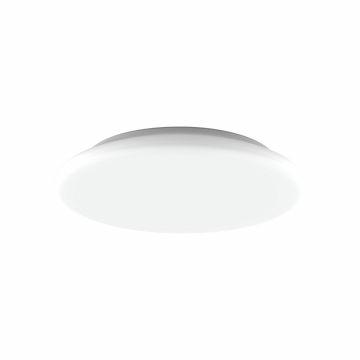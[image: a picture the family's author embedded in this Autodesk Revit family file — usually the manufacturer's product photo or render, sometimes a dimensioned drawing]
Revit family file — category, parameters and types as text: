
# Revit family: Lighting-CommercialSector-GEWISS-ELIA-CL-LED_CEILING_D250
name_source: partatom
category: Apparecchi per illuminazione
units: mm (PartAtom-declared; Revit-internal decimal feet)

## family parameters
Condiviso = No
Host = Superficie
Punto di calcolo locali = Sì
Quota connettore circolare = Usa diametro
Sorgente d'illuminazione = Sì
Taglio con vuoti quando caricato = No
Tipo di parte = Normale

## types (2) — shared parameters
Angolo inclinazione = -90.00°
Application = Indoor
Catalogue = LIGHTING
Catalogue Range = ELIA CL
Colour = White
Colour temperature = 4000K
Colour temperature: = 4000K
Emetti da lunghezza linea = 610 mm
FORO_CONTROSOFFITTO = 80 mm  [stored 0.262467 ft]
File diagramma fotometrico = GWF1315GA840.IES
Filtro dei colori = 16777215
IDF = b5f01b2d-c3ef-4d9d-a266-cfff970ba6d6
IDT = 515d24b2-bb60-4330-99e2-236bf9a850ce
IP degree = IP20 - IP54
Immagine tipo = ELIA_CL.jpg
Installation = Surface mounted
Insulation class = II
LARGHEZZA_FORO = 820 mm
LED = <Per categoria>
LED Life time (L80B50) = L80 B50 (Tq25°) = 50.000h
LUNGHEZZA FORO = 969 mm
L_lampada = 1500 mm
Lamp = LED
Lumen output (lm) = 1150
Operating temperature: = -20° +45°
Optic = Diffusing opal
POSIZIONE = 80000
Produttore = GEWISS S.p.A.
Prospetto di default = 1219 mm
SEO = Surface mounted
STRUTTURA = <Per categoria>
Shock resistance = IK08
System power = 12W
Technical sheet = https://www.gewiss.com
Type of lamp = LED
Type of light source = LED - Not replaceable
Typology = Surface mounted
URL = https://www.gewiss.com
Variazione temperatura colore lampada con luminosità attenuata = <Nessuno>
Version file RFA = 20.0
Voltage = 220-240 VÂ
Warranty = 5 years
Working temperature = -20° +45°

## per-type parameters (varying)
| type | Descrizione | Dimensions (mm) | Modello | Weight (kg) | Weight (kg): |
| GWF1315GA840 - ELIA CL S2 OPAL DIFF 40K ST.ALONE MW | ELIA CL S2 OPAL DIFF 40K ST.ALONE MW | With sensor / Emergency | GWF1315GA840 | 0,9 | 0,9 |
| GWF1310GA840 - ELIA CL S2 OPAL DIFF 40K ST.ALONE ONOFF | ELIA CL S2 OPAL DIFF 40K ST.ALONE ONOFF | Standard | GWF1310GA840 | 0,5 | 0,5 |

note: [stored X ft] marks values corroborated as IEEE doubles in the binary element streams (Revit-internal decimal feet)
